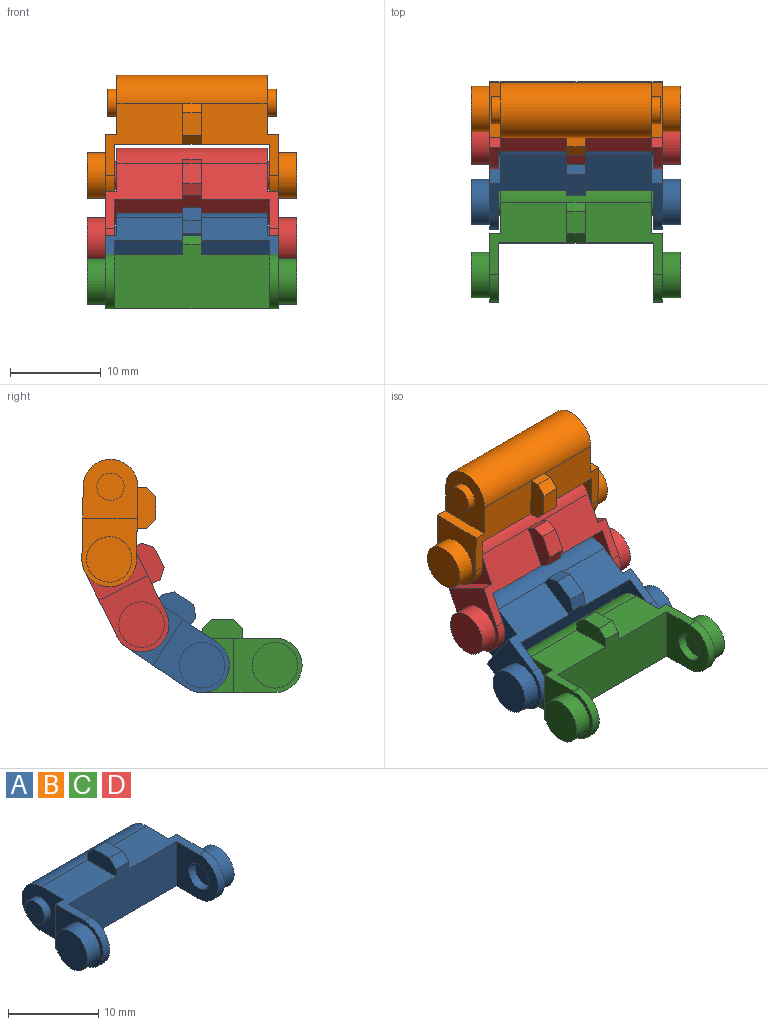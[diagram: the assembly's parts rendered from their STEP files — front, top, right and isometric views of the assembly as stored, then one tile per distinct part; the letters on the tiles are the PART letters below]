
ASSEMBLY  parts=4 mates=3
PART A: 33 faces, bbox 23x14x8 mm
  f0: plane 8.5x8mm, normal (0,0,1), area 37.4mm2, adj f2,f3,f6,f9,f11,f12,f14,f27
  f1: plane 7.5x6mm, normal (1,0,0), area 21.5mm2, adj f7,f8,f10,f13,f25
  f2: plane 7.5x6mm, normal (-1,0,0), area 21.5mm2, adj f0,f7,f9,f12,f22
  f3: plane 6.5x6mm, normal (-1,0,0), area 28.1mm2, adj f0,f7,f9,f14,f19
  f4: plane 6.5x6mm, normal (1,0,0), area 28.1mm2, adj f7,f8,f10,f14,f17
  f5: plane 6.5x6mm, normal (-1,0,0), area 27.1mm2, adj f7,f8,f11,f13,f16
  f6: plane 6.5x6mm, normal (1,0,0), area 27.1mm2, adj f0,f7,f11,f12,f15
  f7: plane 19x8mm, normal (0,0,-1), area 83.8mm2, adj f1,f2,f3,f4,f5,f6,f9,f10
  f8: plane 8.5x8mm, normal (0,0,1), area 37.4mm2, adj f1,f4,f5,f10,f11,f13,f14,f28
  f9: plane 6x1.25mm, normal (0,1,0), area 7.5mm2, adj f0,f2,f3,f7
  f10: plane 6x1.25mm, normal (0,1,0), area 7.5mm2, adj f1,f4,f7,f8
  f11: plane 17x7mm, normal (0,-1,0), area 104mm2, adj f0,f5,f6,f7,f8,f27,f28,f32
  f12: cylinder r=3mm len=6mm, axis (-1,0,0), area 9.4mm2, adj f0,f2,f6,f7
  f13: cylinder r=3mm len=6mm, axis (-1,0,0), area 9.4mm2, adj f1,f5,f7,f8
  f14: cylinder r=3mm len=16.5mm, axis (-1,0,0), area 155.5mm2, adj f0,f3,f4,f7,f8,f29
  f15: cylinder r=1.6mm len=3.2mm, axis (1,0,0), area 10.1mm2, adj f6,f23
  f16: cylinder r=1.6mm len=3.2mm, axis (-1,0,0), area 10.1mm2, adj f5,f26
  f17: cylinder r=1.5mm len=3mm, axis (-1,0,0), area 9.4mm2, adj f4,f18
  f18: plane 3x3mm, normal (1,0,0), area 7.1mm2, adj f17
  f19: cylinder r=1.5mm len=3mm, axis (1,0,0), area 9.4mm2, adj f3,f20
  f20: plane 3x3mm, normal (-1,0,0), area 7.1mm2, adj f19
  f21: plane 5x5mm, normal (-1,0,0), area 19.6mm2, adj f22
  f22: cylinder r=2.5mm len=5mm, axis (1,0,0), area 31.4mm2, adj f2,f21
  f23: plane 3.2x3.2mm, normal (1,0,0), area 8mm2, adj f15
  f24: plane 5x5mm, normal (1,0,0), area 19.6mm2, adj f25
  f25: cylinder r=2.5mm len=5mm, axis (-1,0,0), area 31.4mm2, adj f1,f24
  f26: plane 3.2x3.2mm, normal (-1,0,0), area 8mm2, adj f16
  f27: plane 4.5x2mm, normal (-1,0,0), area 8mm2, adj f0,f11,f29,f30,f31,f32
  f28: plane 4.5x2mm, normal (1,0,0), area 8mm2, adj f8,f11,f29,f30,f31,f32
  f29: plane 2x1mm, normal (0,1,0), area 2mm2, adj f14,f27,f28,f31
  f30: plane 2.5x2mm, normal (0,0,1), area 5mm2, adj f27,f28,f31,f32
  f31: plane 2x1mm, normal (0,0.71,0.71), area 2.8mm2, adj f27,f28,f29,f30
  f32: plane 2x1mm, normal (0,-0.71,0.71), area 2.8mm2, adj f11,f27,f28,f30
PART B: same geometry as A
PART C: same geometry as A
PART D: same geometry as A
PLACE A rot(axis=(1,0,0),34deg) t=(0.17,9.28,0.8)mm
PLACE B rot(axis=(1,0,0),91deg) t=(0.17,17.42,16.74)mm
PLACE C t=(0.17,0.29,-1.95)mm fixed
PLACE D rot(axis=(1,0,0),63.5deg) t=(0.17,15.39,7.77)mm
MATE revolute A.f16 <-> C.f14  axis (-1,0,0) through (9.67,4.29,1.05)mm
MATE revolute B.f16 <-> D.f14  axis (-1,0,0) through (9.67,14.49,12.69)mm
MATE revolute D.f16 <-> A.f14  axis (-1,0,0) through (9.67,10.92,5.53)mm
